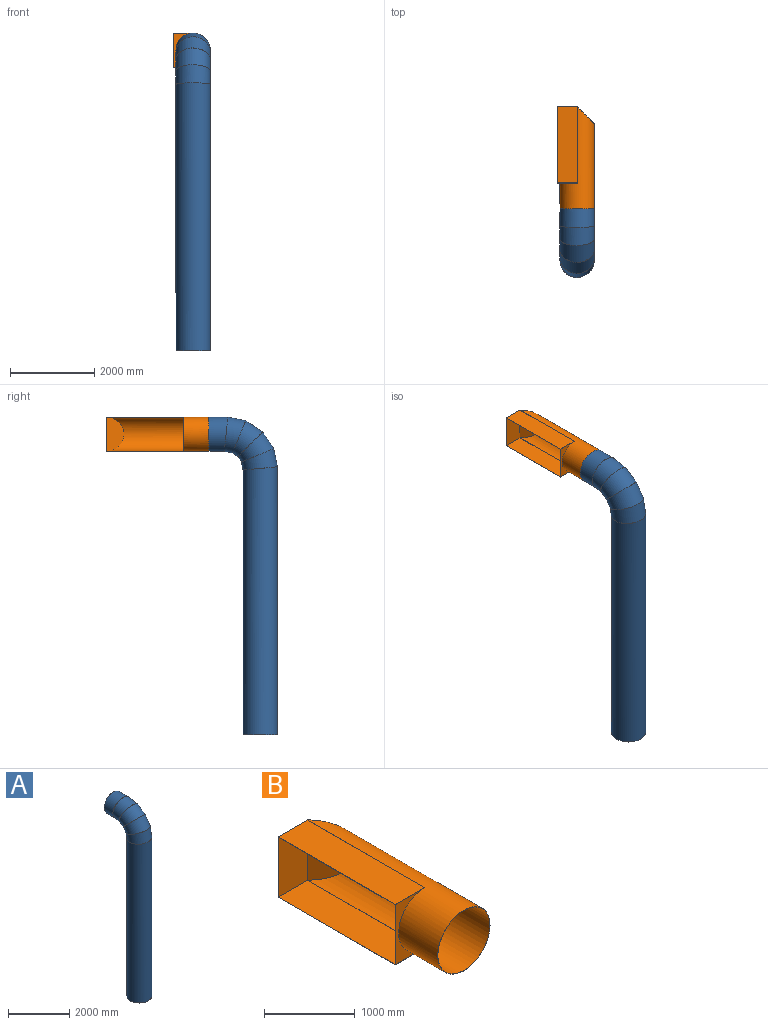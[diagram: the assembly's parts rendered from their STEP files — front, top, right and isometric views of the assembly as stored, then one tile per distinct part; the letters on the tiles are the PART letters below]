
ASSEMBLY  parts=2 mates=1
PART A: 14 faces, bbox 812.8x1625.6x7552.6 mm
  f0: plane 812.8x812.8mm, normal (0,0,-1), area 6465.6mm2, adj f2,f8
  f1: plane 812.8x812.8mm, normal (0,1,0), area 6465.6mm2, adj f7,f13
  f2: cylinder r=406.4mm len=6373.46mm, axis (0,0,-1), area 16168838.6mm2, adj f0,f3
  f3: cylinder r=406.4mm len=882.64mm, axis (0,-0.2,-0.98), area 806322.2mm2, adj f2,f4
  f4: cylinder r=406.4mm len=941.88mm, axis (0,-0.56,-0.83), area 809815.8mm2, adj f3,f5
  f5: cylinder r=406.4mm len=941.88mm, axis (0,-0.83,-0.56), area 809815.8mm2, adj f4,f6
  f6: cylinder r=406.4mm len=882.64mm, axis (0,-0.98,-0.2), area 806322.2mm2, adj f5,f7
  f7: cylinder r=406.4mm len=812.8mm, axis (0,-1,0), area 1034246.5mm2, adj f1,f6
  f8: cylinder r=403.86mm len=6373.41mm, axis (0,0,-1), area 16074701.3mm2, adj f0,f9
  f9: cylinder r=403.86mm len=877.6mm, axis (0,-0.2,-0.98), area 808198.6mm2, adj f8,f10
  f10: cylinder r=403.86mm len=937.35mm, axis (0,-0.56,-0.83), area 804754.1mm2, adj f9,f11
  f11: cylinder r=403.86mm len=937.35mm, axis (0,-0.83,-0.56), area 804754.1mm2, adj f10,f12
  f12: cylinder r=403.86mm len=877.58mm, axis (0,-0.98,-0.2), area 804752.6mm2, adj f11,f13
  f13: cylinder r=403.86mm len=807.72mm, axis (0,-1,0), area 1031252.5mm2, adj f1,f12
PART B: 14 faces, bbox 863.6x2433x812.8 mm
  f0: plane 1823.45x812.8mm, normal (-1,0,0), area 13366.3mm2, adj f1,f2,f3,f4,f8,f9,f10,f11
  f1: plane 812.8x457.2mm, normal (0,-1,0), area 112177.9mm2, adj f0,f2,f3,f6
  f2: plane 1823.45x457.2mm, normal (0,0,1), area 833679.7mm2, adj f0,f1,f4,f6
  f3: plane 1823.45x457.2mm, normal (0,0,-1), area 833679.7mm2, adj f0,f1,f4,f6
  f4: plane 812.8x457.2mm, normal (0,1,0), area 371612.2mm2, adj f0,f2,f3,f5
  f5: plane 812.8x406.4mm, normal (0.71,0.71,0), area 366895.4mm2, adj f4,f6
  f6: cylinder r=406.4mm len=2433.05mm, axis (0,-1,0), area 3554356.3mm2, adj f1,f2,f3,f5,f7
  f7: plane 812.8x812.8mm, normal (0,-1,0), area 6465.6mm2, adj f6,f13
  f8: plane 807.72x457.2mm, normal (0,1,0), area 113088.1mm2, adj f0,f9,f10,f13
  f9: plane 1818.37x457.2mm, normal (0,0,-1), area 831356.5mm2, adj f0,f8,f11,f12,f13
  f10: plane 1818.37x457.2mm, normal (0,0,1), area 831356.5mm2, adj f0,f8,f11,f12,f13
  f11: plane 807.72x456.15mm, normal (0,-1,0), area 368439.8mm2, adj f0,f9,f10,f12
  f12: plane 807.72x404.91mm, normal (-0.71,-0.71,0), area 363525.3mm2, adj f9,f10,f11,f13
  f13: cylinder r=403.86mm len=2429.45mm, axis (0,-1,0), area 3532858.3mm2, adj f7,f8,f9,f10,f12
PLACE A at identity
PLACE B at identity
MATE fastened A.f7 <-> B.f6  axis (0,1,0) through (3784.6,-1521.32,4349.75)mm
